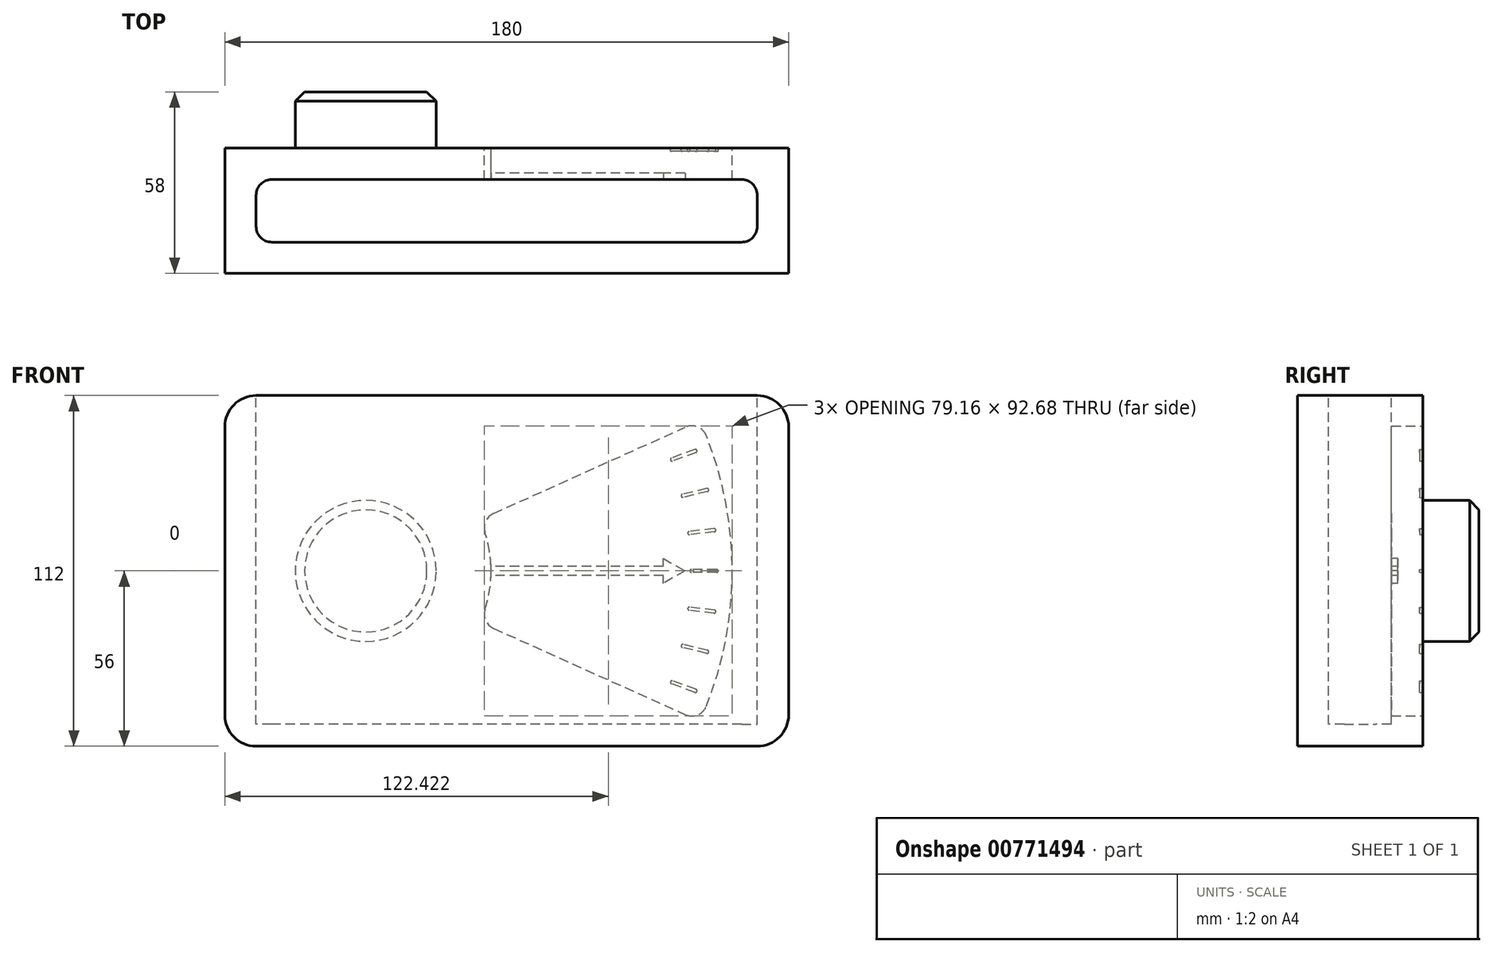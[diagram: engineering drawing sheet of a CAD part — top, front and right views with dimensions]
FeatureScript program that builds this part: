
annotation { "Feature Type Name" : "Feature", "Feature Type Description" : "" }
export const myFeature = defineFeature(function(context is Context, id is Id, definition is map)
    precondition{}
    {
        {
            var Q0;
            Q0=qCreatedBy(makeId("Front.planeOp"),FACE);
            var sketch = newSketch(context, id + "F0", { "sketchPlane" : qUnion([Q0])});
            skLineSegment(sketch, "E0.bottom", {"start": v(-80, 56) * mm, "end": v(80, 56) * mm});
            skLineSegment(sketch, "E0.top", {"start": v(-80, -56) * mm, "end": v(80, -56) * mm});
            skLineSegment(sketch, "E0.left", {"start": v(-90, 46) * mm, "end": v(-90, -46) * mm});
            skLineSegment(sketch, "E0.right", {"start": v(90, 46) * mm, "end": v(90, -46) * mm});
            skPoint(sketch, "E0.middle", {"position": v(0, 0) * mm});
            skLineSegment(sketch, "E1", {"start": v(-90, 0) * mm, "end": v(90, 0) * mm, "construction": true});
            skCircle(sketch, "E2", {"center": v(-45, 0) * mm, "radius": 22.5 * mm});
            skPoint(sketch, "E3.visualSharp", {"position": v(-90, 56) * mm});
            skArc(sketch, "E3.filletArc", {"start": v(-80, 56) * mm, "mid": v(-87.07, 53.07) * mm, "end": v(-90, 46) * mm});
            skPoint(sketch, "E4.visualSharp", {"position": v(-90, -56) * mm});
            skArc(sketch, "E4.filletArc", {"start": v(-90, -46) * mm, "mid": v(-87.07, -53.07) * mm, "end": v(-80, -56) * mm});
            skPoint(sketch, "E5.visualSharp", {"position": v(90, -56) * mm});
            skArc(sketch, "E5.filletArc", {"start": v(80, -56) * mm, "mid": v(87.07, -53.07) * mm, "end": v(90, -46) * mm});
            skPoint(sketch, "E6.visualSharp", {"position": v(90, 56) * mm});
            skArc(sketch, "E6.filletArc", {"start": v(90, 46) * mm, "mid": v(87.07, 53.07) * mm, "end": v(80, 56) * mm});
            skLineSegment(sketch, "E7", {"start": v(-12.5, 56) * mm, "end": v(-12.5, -56) * mm, "construction": true});
            skArc(sketch, "E8", {"start": v(63.74, -43.19) * mm, "mid": v(72, 0) * mm, "end": v(63.74, 43.19) * mm});
            skLineSegment(sketch, "E9", {"start": v(-4.22, 18.35) * mm, "end": v(57.04, 45.9) * mm});
            skLineSegment(sketch, "E10", {"start": v(-4.22, -18.35) * mm, "end": v(57.04, -45.9) * mm});
            skArc(sketch, "E11", {"start": v(-6.92, -12.26) * mm, "mid": v(-5, 0) * mm, "end": v(-6.92, 12.26) * mm});
            skPoint(sketch, "E12.visualSharp", {"position": v(61.7, 48) * mm});
            skArc(sketch, "E12.filletArc", {"start": v(63.74, 43.19) * mm, "mid": v(60.97, 45.98) * mm, "end": v(57.04, 45.9) * mm});
            skPoint(sketch, "E13.visualSharp", {"position": v(61.7, -48) * mm});
            skArc(sketch, "E13.filletArc", {"start": v(57.04, -45.9) * mm, "mid": v(60.97, -45.98) * mm, "end": v(63.74, -43.19) * mm});
            skArc(sketch, "E14.filletArc", {"start": v(-6.92, -12.26) * mm, "mid": v(-6.73, -15.82) * mm, "end": v(-4.22, -18.35) * mm});
            skArc(sketch, "E15.filletArc", {"start": v(-4.22, 18.35) * mm, "mid": v(-6.73, 15.82) * mm, "end": v(-6.92, 12.26) * mm});
            skSolve(sketch);
        }
        {
            var Q0;
            Q0=makeQuery(id+"F0.imprint","IMPRINT",FACE,{"disambiguationData":[TD([[makeQuery(id+"F0.imprint","IMPRINT",EDGE,{"derivedFrom":sQuery(id+"F0.wireOp",EDGE,"E0.bottom")}),-1.0]])]});
            var Q1;
            Q1=makeQuery(id+"F0.imprint","IMPRINT",FACE,{"disambiguationData":[TD([[makeQuery(id+"F0.imprint","IMPRINT",EDGE,{"derivedFrom":sQuery(id+"F0.wireOp",EDGE,"E0.left")}),1.0]])]});
            var Q2;
            {var subQ5=sQuery(id+"F0.wireOp",EDGE,"3kxiyQwo-XHE4-hQme-LXMz-W8Swnx3x74QT");Q2=makeQuery(id+"F0.imprint","IMPRINT",FACE,{"disambiguationData":[TD([[makeQuery(id+"F0.imprint","IMPRINT",EDGE,{"derivedFrom":subQ5}),1.0]])]});}
            var Q3;
            {var subQ1=sQuery(id+"F0.wireOp",EDGE,"E2");var subQ6=sQuery(id+"F0.wireOp",EDGE,"WLCiJla5-Rco1-iDx6-f8Mr-UCqioGqXZ493");var subQ8=makeQuery(id+"F0.imprint","INTERSECT",VERTEX,{"derivedFrom":[subQ1,subQ6]});Q3=makeQuery(id+"F0.imprint","IMPRINT",FACE,{"disambiguationData":[TD([[makeQuery(id+"F0.imprint","IMPRINT",EDGE,{"disambiguationData":[TD([[subQ8,-1.0]])],"derivedFrom":subQ1}),-1.0]])]});}
            var Q4;
            {var subQ0=sQuery(id+"F0.wireOp",EDGE,"Uy5Vi2SS-7DH2-u9qp-6SYO-DGrq1o2wwcIu");var subQ1=sQuery(id+"F0.wireOp",EDGE,"E2");var subQ2=makeQuery(id+"F0.imprint","INTERSECT",VERTEX,{"derivedFrom":[subQ1,subQ0]});Q4=makeQuery(id+"F0.imprint","IMPRINT",FACE,{"disambiguationData":[TD([[makeQuery(id+"F0.imprint","IMPRINT",EDGE,{"disambiguationData":[TD([[subQ2,-1.0]])],"derivedFrom":subQ1}),-1.0]])]});}
            var Q5;
            {var subQ0=sQuery(id+"F0.wireOp",EDGE,"E9");var subQ1=sQuery(id+"F0.wireOp",EDGE,"E2");var subQ2=makeQuery(id+"F0.imprint","INTERSECT",VERTEX,{"derivedFrom":[subQ1,subQ0]});Q5=makeQuery(id+"F0.imprint","IMPRINT",FACE,{"disambiguationData":[TD([[makeQuery(id+"F0.imprint","IMPRINT",EDGE,{"disambiguationData":[TD([[subQ2,1.0]])],"derivedFrom":subQ1}),-1.0]])]});}
            var Q6;
            {var subQ0=sQuery(id+"F0.wireOp",EDGE,"WLCiJla5-Rco1-iDx6-f8Mr-UCqioGqXZ493");var subQ1=sQuery(id+"F0.wireOp",EDGE,"E2");var subQ2=makeQuery(id+"F0.imprint","INTERSECT",VERTEX,{"derivedFrom":[subQ1,subQ0]});Q6=makeQuery(id+"F0.imprint","IMPRINT",FACE,{"disambiguationData":[TD([[makeQuery(id+"F0.imprint","IMPRINT",EDGE,{"disambiguationData":[TD([[subQ2,1.0]])],"derivedFrom":subQ1}),-1.0]])]});}
            var Q7;
            Q7=makeQuery(id+"F0.imprint","IMPRINT",FACE,{"disambiguationData":[TD([[makeQuery(id+"F0.imprint","IMPRINT",EDGE,{"derivedFrom":sQuery(id+"F0.wireOp",EDGE,"E0.right")}),-1.0]])]});
            var Q8;
            {var subQ0=sQuery(id+"F0.wireOp",EDGE,"E8");Q8=makeQuery(id+"F0.imprint","IMPRINT",FACE,{"disambiguationData":[TD([[makeQuery(id+"F0.imprint","IMPRINT",EDGE,{"derivedFrom":subQ0}),1.0]])]});}
            var Q9;
            {var subQ0=sQuery(id+"F0.wireOp",EDGE,"E9");var subQ1=sQuery(id+"F0.wireOp",EDGE,"E2");var subQ2=makeQuery(id+"F0.imprint","INTERSECT",VERTEX,{"derivedFrom":[subQ1,subQ0]});Q9=makeQuery(id+"F0.imprint","IMPRINT",FACE,{"disambiguationData":[TD([[makeQuery(id+"F0.imprint","IMPRINT",EDGE,{"disambiguationData":[TD([[subQ2,-1.0]])],"derivedFrom":subQ1}),1.0]])]});}
            var Q10;
            {var subQ0=sQuery(id+"F0.wireOp",EDGE,"E9");var subQ1=sQuery(id+"F0.wireOp",EDGE,"E2");var subQ2=makeQuery(id+"F0.imprint","INTERSECT",VERTEX,{"derivedFrom":[subQ1,subQ0]});Q10=makeQuery(id+"F0.imprint","IMPRINT",FACE,{"disambiguationData":[TD([[makeQuery(id+"F0.imprint","IMPRINT",EDGE,{"disambiguationData":[TD([[subQ2,1.0]])],"derivedFrom":subQ1}),1.0]])]});}
            extrude(context, id + "F1", {"entities" : qUnion([Q0, Q1, Q2, Q3, Q4, Q5, Q6, Q7, Q8, Q9, Q10]), "depth" : 40 * mm, "offsetDistance" : 25 * mm});
        }
        {
            var Q0;
            {var subQ0=sQuery(id+"F0.wireOp",EDGE,"E8");Q0=makeQuery(id+"F0.imprint","IMPRINT",FACE,{"disambiguationData":[TD([[makeQuery(id+"F0.imprint","IMPRINT",EDGE,{"derivedFrom":subQ0}),1.0]])]});}
            extrude(context, id + "F2", {"entities" : qUnion([Q0]), "operationType" : NewBodyOperationType.REMOVE, "depth" : 12 * mm, "offsetDistance" : 25 * mm});
        }
        {
            var Q0;
            {var subQ0=sQuery(id+"F0.wireOp",EDGE,"E9");var subQ1=sQuery(id+"F0.wireOp",EDGE,"E2");var subQ2=makeQuery(id+"F0.imprint","INTERSECT",VERTEX,{"derivedFrom":[subQ1,subQ0]});Q0=makeQuery(id+"F0.imprint","IMPRINT",FACE,{"disambiguationData":[TD([[makeQuery(id+"F0.imprint","IMPRINT",EDGE,{"disambiguationData":[TD([[subQ2,-1.0]])],"derivedFrom":subQ1}),1.0]])]});}
            var Q1;
            {var subQ0=sQuery(id+"F0.wireOp",EDGE,"E9");var subQ1=sQuery(id+"F0.wireOp",EDGE,"E2");var subQ2=makeQuery(id+"F0.imprint","INTERSECT",VERTEX,{"derivedFrom":[subQ1,subQ0]});Q1=makeQuery(id+"F0.imprint","IMPRINT",FACE,{"disambiguationData":[TD([[makeQuery(id+"F0.imprint","IMPRINT",EDGE,{"disambiguationData":[TD([[subQ2,1.0]])],"derivedFrom":subQ1}),1.0]])]});}
            extrude(context, id + "F3", {"entities" : qUnion([Q0, Q1]), "oppositeDirection" : true, "depth" : 18 * mm, "offsetDistance" : 25 * mm});
        }
        {
            var Q0;
            Q0=makeQuery(id+"F3.opExtrude","CAP_EDGE",EDGE,{"disambiguationData":[OSD([sQuery(id+"F0.wireOp",EDGE,"E2")])],"isStart":false});
            chamfer(context, id + "F4", {"entities" : qUnion([Q0]), "width" : 3 * mm, "tangentPropagation" : true});
        }
        {
            var Q0;
            Q0=makeQuery(id+"F1.opExtrude","SWEPT_FACE",FACE,{"disambiguationData":[OSD([sQuery(id+"F0.wireOp",EDGE,"E0.bottom")])]});
            var sketch = newSketch(context, id + "F5", { "sketchPlane" : qUnion([Q0])});
            skLineSegment(sketch, "E16.bottom", {"start": v(80, -30) * mm, "end": v(-80, -30) * mm});
            skLineSegment(sketch, "E16.top", {"start": v(80, -10) * mm, "end": v(-80, -10) * mm});
            skLineSegment(sketch, "E16.left", {"start": v(80, -30) * mm, "end": v(80, -10) * mm});
            skLineSegment(sketch, "E16.right", {"start": v(-80, -30) * mm, "end": v(-80, -10) * mm});
            skSolve(sketch);
        }
        {
            var Q0;
            Q0=makeQuery(id+"F5.imprint","IMPRINT",FACE,{"disambiguationData":[TD([[makeQuery(id+"F5.imprint","IMPRINT",EDGE,{"derivedFrom":sQuery(id+"F5.wireOp",EDGE,"E16.bottom")}),-1.0]])]});
            extrude(context, id + "F6", {"entities" : qUnion([Q0]), "operationType" : NewBodyOperationType.REMOVE, "oppositeDirection" : true, "depth" : 105 * mm, "offsetDistance" : 25 * mm});
        }
        {
            var Q0;
            {var subQ0=sQuery(id+"F0.wireOp",EDGE,"E8");Q0=makeQuery(id+"F0.imprint","IMPRINT",FACE,{"disambiguationData":[TD([[makeQuery(id+"F0.imprint","IMPRINT",EDGE,{"derivedFrom":subQ0}),1.0]])]});}
            extrude(context, id + "F7", {"entities" : qUnion([Q0]), "depth" : 10 * mm, "offsetDistance" : 25 * mm});
        }
        {
            var Q0;
            Q0=makeQuery(id+"F6.boolean.opBoolean","COPY",EDGE,{"derivedFrom":makeQuery(id+"F6.opExtrude","SWEPT_EDGE",EDGE,{"disambiguationData":[OSD([sQuery(id+"F0.wireOp",EDGE,"E0.bottom"),sQuery(id+"F0.wireOp",EDGE,"E6.filletArc"),sQuery(id+"F5.wireOp",EDGE,"E16.bottom"),sQuery(id+"F5.wireOp",EDGE,"E16.left")])]})});
            var Q1;
            Q1=makeQuery(id+"F6.boolean.opBoolean","COPY",EDGE,{"derivedFrom":makeQuery(id+"F6.opExtrude","SWEPT_EDGE",EDGE,{"disambiguationData":[OSD([sQuery(id+"F0.wireOp",EDGE,"E0.bottom"),sQuery(id+"F0.wireOp",EDGE,"E6.filletArc"),sQuery(id+"F5.wireOp",EDGE,"E16.top"),sQuery(id+"F5.wireOp",EDGE,"E16.left")])]})});
            var Q2;
            Q2=makeQuery(id+"F6.boolean.opBoolean","COPY",EDGE,{"derivedFrom":makeQuery(id+"F6.opExtrude","SWEPT_EDGE",EDGE,{"disambiguationData":[OSD([sQuery(id+"F0.wireOp",EDGE,"E0.bottom"),sQuery(id+"F0.wireOp",EDGE,"E3.filletArc"),sQuery(id+"F5.wireOp",EDGE,"E16.bottom"),sQuery(id+"F5.wireOp",EDGE,"E16.right")])]})});
            var Q3;
            Q3=makeQuery(id+"F6.boolean.opBoolean","COPY",EDGE,{"derivedFrom":makeQuery(id+"F6.opExtrude","SWEPT_EDGE",EDGE,{"disambiguationData":[OSD([sQuery(id+"F0.wireOp",EDGE,"E0.bottom"),sQuery(id+"F0.wireOp",EDGE,"E3.filletArc"),sQuery(id+"F5.wireOp",EDGE,"E16.top"),sQuery(id+"F5.wireOp",EDGE,"E16.right")])]})});
            fillet(context, id + "F8", {"entities" : qUnion([Q0, Q1, Q2, Q3]), "radius" : 5 * mm, "tangentPropagation" : true, "allowEdgeOverflow" : false});
        }
        {
            var Q0;
            Q0=makeQuery(id+"F0.imprint","IMPRINT",FACE,{"disambiguationData":[TD([[makeQuery(id+"F0.imprint","IMPRINT",EDGE,{"derivedFrom":sQuery(id+"F0.wireOp",EDGE,"E8")}),1.0]])]});
            var sketch = newSketch(context, id + "F9", { "sketchPlane" : qUnion([Q0])});
            skLineSegment(sketch, "E17.0", {"start": v(-4.22, 18.35) * mm, "end": v(57.04, 45.9) * mm, "construction": true});
            skPoint(sketch, "E18.0", {"position": v(26.41, -32.13) * mm});
            skLineSegment(sketch, "E19.0", {"start": v(-4.22, -18.35) * mm, "end": v(57.04, -45.9) * mm, "construction": true});
            skArc(sketch, "E20.0", {"start": v(-6.92, -12.26) * mm, "mid": v(-5, 0) * mm, "end": v(-6.92, 12.26) * mm, "construction": true});
            skPoint(sketch, "E21.0", {"position": v(-6.73, -15.82) * mm});
            skPoint(sketch, "E22.0", {"position": v(-6.73, 15.82) * mm});
            skArc(sketch, "E23.0", {"start": v(-4.22, 18.35) * mm, "mid": v(-6.73, 15.82) * mm, "end": v(-6.92, 12.26) * mm, "construction": true});
            skArc(sketch, "E24.0", {"start": v(-6.92, -12.26) * mm, "mid": v(-6.73, -15.82) * mm, "end": v(-4.22, -18.35) * mm, "construction": true});
            skArc(sketch, "E25.0", {"start": v(63.74, -43.19) * mm, "mid": v(72, 0) * mm, "end": v(63.74, 43.19) * mm, "construction": true});
            skArc(sketch, "E26.0", {"start": v(63.74, 43.19) * mm, "mid": v(60.97, 45.98) * mm, "end": v(57.04, 45.9) * mm, "construction": true});
            skArc(sketch, "E27.0", {"start": v(57.04, -45.9) * mm, "mid": v(60.97, -45.98) * mm, "end": v(63.74, -43.19) * mm, "construction": true});
            skLineSegment(sketch, "E28", {"start": v(67, 0) * mm, "end": v(59, 0) * mm});
            skArc(sketch, "E29.0.startCap", {"start": v(67, 0.5) * mm, "mid": v(67.5, 0) * mm, "end": v(67, -0.5) * mm});
            skArc(sketch, "E29.0.endCap", {"start": v(59, -0.5) * mm, "mid": v(58.5, 0) * mm, "end": v(59, 0.5) * mm});
            skLineSegment(sketch, "E29.0.left", {"start": v(67, -0.5) * mm, "end": v(59, -0.5) * mm});
            skLineSegment(sketch, "E29.0.right", {"start": v(67, 0.5) * mm, "end": v(59, 0.5) * mm});
            skPoint(sketch, "E30.center", {"position": v(0, 0) * mm});
            skLineSegment(sketch, "E31.1.0", {"start": v(66.18, -13.5) * mm, "end": v(58.24, -12.57) * mm});
            skArc(sketch, "E31.1.1", {"start": v(66.3, -12.5) * mm, "mid": v(66.74, -13.06) * mm, "end": v(66.18, -13.5) * mm});
            skLineSegment(sketch, "E31.1.2", {"start": v(66.3, -12.5) * mm, "end": v(58.35, -11.58) * mm});
            skArc(sketch, "E31.1.3", {"start": v(58.24, -12.57) * mm, "mid": v(57.8, -12.02) * mm, "end": v(58.35, -11.58) * mm});
            skLineSegment(sketch, "E31.2.0", {"start": v(63.87, -26.32) * mm, "end": v(56.08, -24.47) * mm});
            skArc(sketch, "E31.2.1", {"start": v(64.1, -25.34) * mm, "mid": v(64.47, -25.94) * mm, "end": v(63.87, -26.32) * mm});
            skLineSegment(sketch, "E31.2.2", {"start": v(64.1, -25.34) * mm, "end": v(56.31, -23.5) * mm});
            skArc(sketch, "E31.2.3", {"start": v(56.08, -24.47) * mm, "mid": v(55.71, -23.87) * mm, "end": v(56.31, -23.5) * mm});
            skLineSegment(sketch, "E31.3.0", {"start": v(60.07, -38.78) * mm, "end": v(52.56, -36.04) * mm});
            skArc(sketch, "E31.3.1", {"start": v(60.42, -37.84) * mm, "mid": v(60.72, -38.48) * mm, "end": v(60.07, -38.78) * mm});
            skLineSegment(sketch, "E31.3.2", {"start": v(60.42, -37.84) * mm, "end": v(52.9, -35.1) * mm});
            skArc(sketch, "E31.3.3", {"start": v(52.56, -36.04) * mm, "mid": v(52.26, -35.4) * mm, "end": v(52.9, -35.1) * mm});
            skLineSegment(sketch, "E31.anchor1", {"start": v(-45, 0) * mm, "end": v(59, -0.5) * mm, "construction": true});
            skLineSegment(sketch, "E31.anchor2", {"start": v(-45, 0) * mm, "end": v(52.56, -36.04) * mm, "construction": true});
            skLineSegment(sketch, "E32.1.0", {"start": v(66.18, 13.5) * mm, "end": v(58.24, 12.57) * mm});
            skLineSegment(sketch, "E32.1.1", {"start": v(66.3, 12.5) * mm, "end": v(58.35, 11.58) * mm});
            skArc(sketch, "E32.1.2", {"start": v(66.18, 13.5) * mm, "mid": v(66.74, 13.06) * mm, "end": v(66.3, 12.5) * mm});
            skArc(sketch, "E32.1.3", {"start": v(58.35, 11.58) * mm, "mid": v(57.8, 12.02) * mm, "end": v(58.24, 12.57) * mm});
            skArc(sketch, "E32.1.4", {"start": v(68.02, -30.27) * mm, "mid": v(71.2, 13.58) * mm, "end": v(57.99, 55.52) * mm, "construction": true});
            skLineSegment(sketch, "E32.2.0", {"start": v(63.87, 26.32) * mm, "end": v(56.08, 24.47) * mm});
            skLineSegment(sketch, "E32.2.1", {"start": v(64.1, 25.34) * mm, "end": v(56.31, 23.5) * mm});
            skArc(sketch, "E32.2.2", {"start": v(63.87, 26.32) * mm, "mid": v(64.47, 25.94) * mm, "end": v(64.1, 25.34) * mm});
            skArc(sketch, "E32.2.3", {"start": v(56.31, 23.5) * mm, "mid": v(55.71, 23.87) * mm, "end": v(56.08, 24.47) * mm});
            skArc(sketch, "E32.2.4", {"start": v(70.77, -16.95) * mm, "mid": v(68.85, 26.98) * mm, "end": v(50.85, 67.1) * mm, "construction": true});
            skLineSegment(sketch, "E32.3.0", {"start": v(60.07, 38.78) * mm, "end": v(52.56, 36.04) * mm});
            skLineSegment(sketch, "E32.3.1", {"start": v(60.42, 37.84) * mm, "end": v(52.9, 35.1) * mm});
            skArc(sketch, "E32.3.2", {"start": v(60.07, 38.78) * mm, "mid": v(60.72, 38.48) * mm, "end": v(60.42, 37.84) * mm});
            skArc(sketch, "E32.3.3", {"start": v(52.9, 35.1) * mm, "mid": v(52.26, 35.4) * mm, "end": v(52.56, 36.04) * mm});
            skArc(sketch, "E32.3.4", {"start": v(71.95, -3.4) * mm, "mid": v(64.94, 40.02) * mm, "end": v(42.4, 77.77) * mm, "construction": true});
            skLineSegment(sketch, "E32.anchor1", {"start": v(-45, 0) * mm, "end": v(59, 0.5) * mm, "construction": true});
            skLineSegment(sketch, "E32.anchor2", {"start": v(-45, 0) * mm, "end": v(52.56, 36.04) * mm, "construction": true});
            skSolve(sketch);
        }
        {
            var Q0;
            Q0 = qSketchRegion(id + "F9", true);
            extrude(context, id + "F10", {"entities" : qUnion([Q0]), "operationType" : NewBodyOperationType.REMOVE, "depth" : 1 * mm, "offsetDistance" : 25 * mm});
        }
        {
            var Q0;
            Q0 = qSketchRegion(id + "F9", true);
            extrude(context, id + "F11", {"entities" : qUnion([Q0]), "depth" : 1 * mm, "offsetDistance" : 25 * mm});
        }
        {
            var Q0;
            Q0=makeQuery(id+"F7.opExtrude","CAP_FACE",FACE,{"disambiguationData":[OSD([sQuery(id+"F0.wireOp",EDGE,"E8"),sQuery(id+"F0.wireOp",EDGE,"E9"),sQuery(id+"F0.wireOp",EDGE,"E10"),sQuery(id+"F0.wireOp",EDGE,"E11"),sQuery(id+"F0.wireOp",EDGE,"E12.filletArc"),sQuery(id+"F0.wireOp",EDGE,"E13.filletArc"),sQuery(id+"F0.wireOp",EDGE,"E14.filletArc"),sQuery(id+"F0.wireOp",EDGE,"E15.filletArc")])],"isStart":false});
            var sketch = newSketch(context, id + "F12", { "sketchPlane" : qUnion([Q0])});
            skLineSegment(sketch, "E33", {"start": v(49.97, -1.5) * mm, "end": v(-5.03, -1.5) * mm});
            skLineSegment(sketch, "E34", {"start": v(49.97, 1.5) * mm, "end": v(-5.03, 1.5) * mm});
            skLineSegment(sketch, "E35", {"start": v(56.97, 0) * mm, "end": v(49.97, -4) * mm});
            skLineSegment(sketch, "E36", {"start": v(49.97, -4) * mm, "end": v(49.97, -1.5) * mm});
            skLineSegment(sketch, "E37", {"start": v(49.97, 1.5) * mm, "end": v(49.97, 4) * mm});
            skLineSegment(sketch, "E38", {"start": v(49.97, 4) * mm, "end": v(56.97, 0) * mm});
            skArc(sketch, "E39.0", {"start": v(-5.03, 1.5) * mm, "mid": v(-5, 0) * mm, "end": v(-5.03, -1.5) * mm});
            skPoint(sketch, "E40.orphan", {"position": v(-6.92, 12.26) * mm});
            skPoint(sketch, "E41.orphan", {"position": v(-6.92, -12.26) * mm});
            skSolve(sketch);
        }
        {
            var Q0;
            {var subQ1=sQuery(id+"F12.wireOp",EDGE,"E33");Q0=makeQuery(id+"F12.imprint","IMPRINT",FACE,{"disambiguationData":[TD([[makeQuery(id+"F12.imprint","IMPRINT",EDGE,{"derivedFrom":subQ1}),-1.0]])]});}
            extrude(context, id + "F13", {"entities" : qUnion([Q0]), "operationType" : NewBodyOperationType.REMOVE, "oppositeDirection" : true, "depth" : 2 * mm, "offsetDistance" : 25 * mm});
        }
        {
            var Q0;
            Q0 = qSketchRegion(id + "F12", true);
            extrude(context, id + "F14", {"entities" : qUnion([Q0]), "oppositeDirection" : true, "depth" : 2 * mm, "offsetDistance" : 25 * mm});
        }
    });
